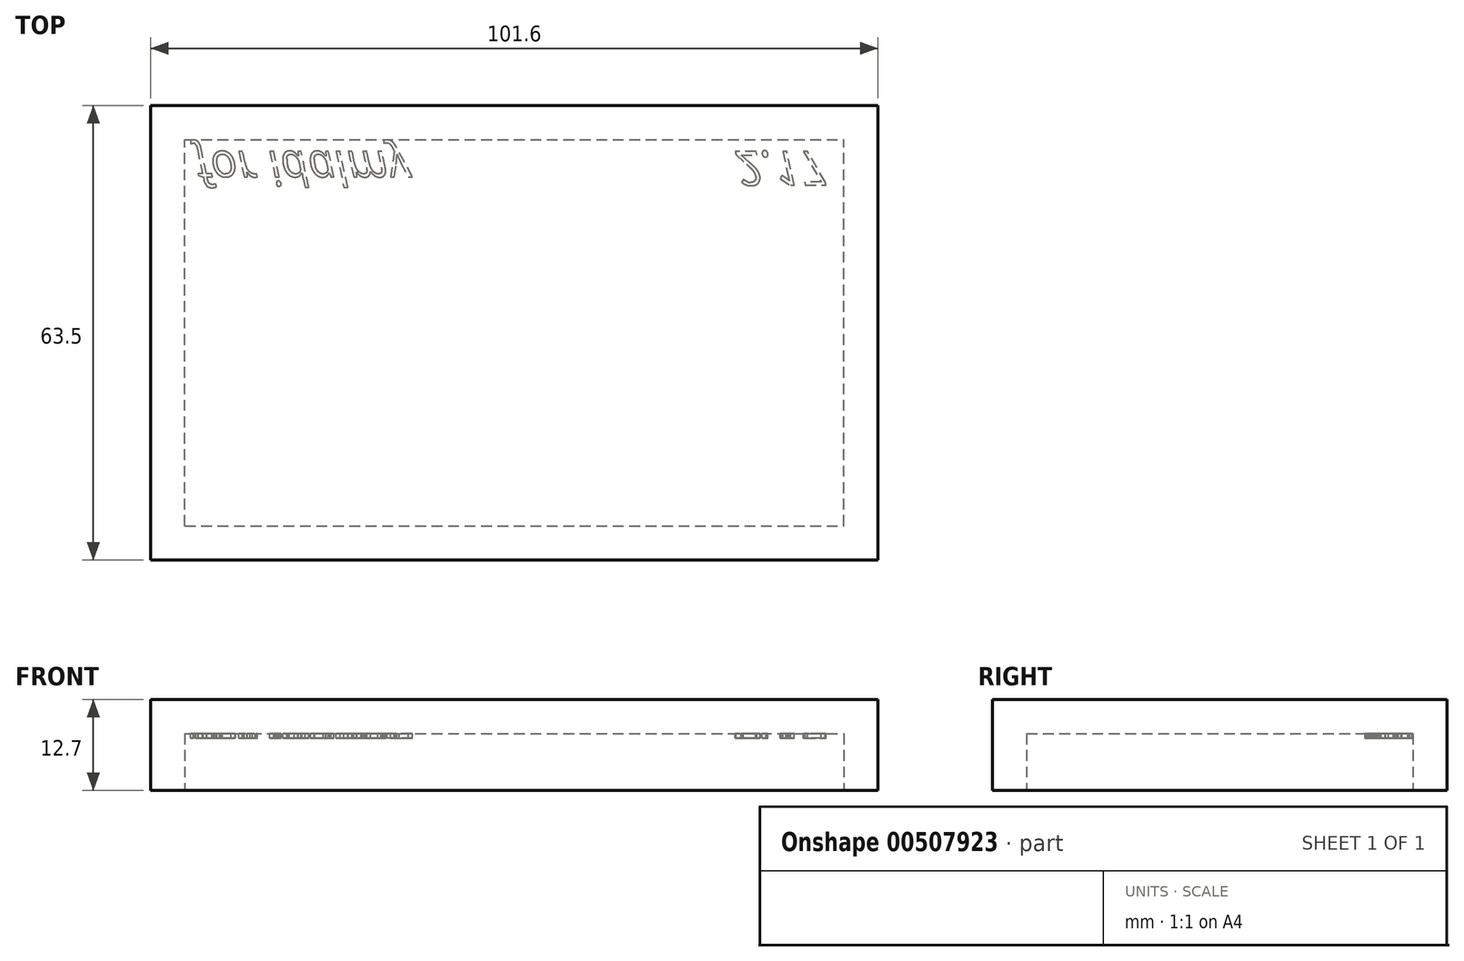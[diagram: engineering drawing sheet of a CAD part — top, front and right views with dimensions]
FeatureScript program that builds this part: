
annotation { "Feature Type Name" : "Feature", "Feature Type Description" : "" }
export const myFeature = defineFeature(function(context is Context, id is Id, definition is map)
    precondition{}
    {
        {
            var Q0;
            Q0=qCreatedBy(makeId("Top.planeOp"),FACE);
            var sketch = newSketch(context, id + "F0", { "sketchPlane" : qUnion([Q0])});
            skLineSegment(sketch, "E0.bottom", {"start": v(-50.8, -31.75) * mm, "end": v(50.8, -31.75) * mm});
            skLineSegment(sketch, "E0.top", {"start": v(-50.8, 31.75) * mm, "end": v(50.8, 31.75) * mm});
            skLineSegment(sketch, "E0.left", {"start": v(-50.8, -31.75) * mm, "end": v(-50.8, 31.75) * mm});
            skLineSegment(sketch, "E0.right", {"start": v(50.8, -31.75) * mm, "end": v(50.8, 31.75) * mm});
            skSolve(sketch);
        }
        {
            var Q0;
            Q0=makeQuery(id+"F0.imprint","IMPRINT",FACE,{"disambiguationData":[TD([[makeQuery(id+"F0.imprint","IMPRINT",EDGE,{"derivedFrom":sQuery(id+"F0.wireOp",EDGE,"E0.bottom")}),1.0]])]});
            extrude(context, id + "F1", {"entities" : qUnion([Q0]), "depth" : 12.7 * mm});
        }
        {
            var Q0;
            Q0=makeQuery(id+"F1.opExtrude","CAP_FACE",FACE,{"disambiguationData":[OSD([sQuery(id+"F0.wireOp",EDGE,"E0.bottom"),sQuery(id+"F0.wireOp",EDGE,"E0.top"),sQuery(id+"F0.wireOp",EDGE,"E0.left"),sQuery(id+"F0.wireOp",EDGE,"E0.right")])],"isStart":true});
            shell(context, id + "F2", {"entities" : qUnion([Q0]), "thickness" : 4.76 * mm});
        }
        {
            var Q0;
            Q0=makeQuery(id+"F2.opShell","OFFSET_FACE",FACE,{"disambiguationData":[OSD([sQuery(id+"F0.wireOp",EDGE,"E0.bottom"),sQuery(id+"F0.wireOp",EDGE,"E0.top"),sQuery(id+"F0.wireOp",EDGE,"E0.left"),sQuery(id+"F0.wireOp",EDGE,"E0.right")])]});
            var sketch = newSketch(context, id + "F3", { "sketchPlane" : qUnion([Q0])});
            skText(sketch, "E1", { "text": "for idalmy", "fontName": "OpenSans-Italic.ttf"});
            skText(sketch, "E2", { "text": "2.17", "fontName": "OpenSans-Italic.ttf"});
            const initialGuessF3  = {"E1": [-0.0445, -0.02535, 1, 0, 0.00478], "E2": [0.03083, -0.02535, 1, 0, 0.00478]};
            skSetInitialGuess(sketch, initialGuessF3);
            skSolve(sketch);
        }
        {
            var Q0;
            Q0 = qSketchRegion(id + "F3", true);
            extrude(context, id + "F4", {"entities" : qUnion([Q0]), "operationType" : NewBodyOperationType.ADD, "depth" : 0.64 * mm});
        }
    });
